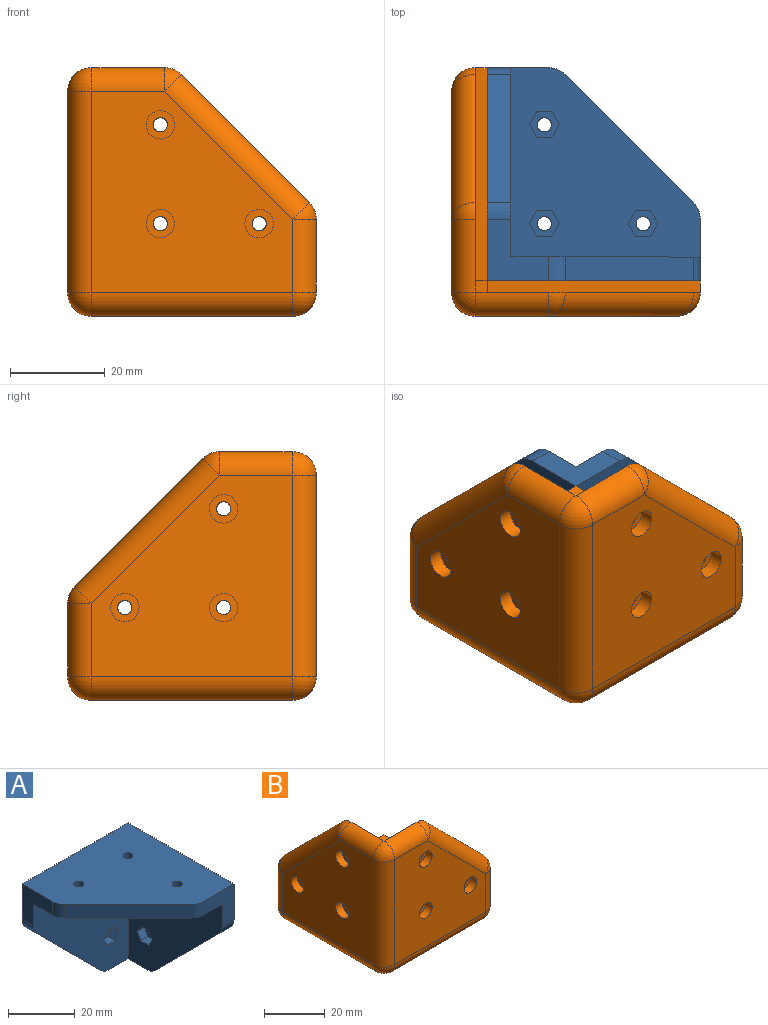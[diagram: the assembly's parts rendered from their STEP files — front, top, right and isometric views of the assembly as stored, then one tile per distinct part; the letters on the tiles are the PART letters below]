
ASSEMBLY  parts=2 mates=1
PART A: 90 faces, bbox 45x45x45 mm
  f0: plane 40x40mm, normal (0,0,-1), area 1070.3mm2, adj f1,f2,f3,f5,f9,f57,f58,f59
  f1: plane 40x40mm, normal (0,-1,0), area 1070.3mm2, adj f0,f2,f5,f6,f10,f36,f37,f38
  f2: plane 40x40mm, normal (-1,0,0), area 1070.3mm2, adj f0,f1,f3,f6,f11,f12,f13,f14
  f3: plane 12.93x12.93mm, normal (0,-1,0), area 104.3mm2, adj f0,f2,f4,f7,f84,f89
  f4: plane 45x45mm, normal (1,0,0), area 1552.7mm2, adj f3,f6,f7,f8,f11,f33,f34,f35
  f5: plane 12.93x12.93mm, normal (-1,0,0), area 104.3mm2, adj f0,f1,f7,f8,f86,f88
  f6: plane 12.93x12.93mm, normal (0,0,-1), area 104.3mm2, adj f1,f2,f4,f8,f85,f87
  f7: plane 45x45mm, normal (0,0,1), area 1552.7mm2, adj f3,f4,f5,f8,f9,f78,f79,f80
  f8: plane 45x45mm, normal (0,1,0), area 1552.7mm2, adj f4,f5,f6,f7,f10,f81,f82,f83
  f9: plane 27.07x27.07mm, normal (-0.71,-0.71,0), area 191.4mm2, adj f0,f7,f88,f89
  f10: plane 27.07x27.07mm, normal (-0.71,0,-0.71), area 191.4mm2, adj f1,f8,f86,f87
  f11: plane 27.07x27.07mm, normal (0,-0.71,-0.71), area 191.4mm2, adj f2,f4,f84,f85
  f12: plane 3x2.75mm, normal (0,0.87,-0.5), area 9.5mm2, adj f2,f13,f17,f18
  f13: plane 3.18x3mm, normal (0,0,-1), area 9.5mm2, adj f2,f12,f14,f18
  f14: plane 3x2.75mm, normal (0,-0.87,-0.5), area 9.5mm2, adj f2,f13,f15,f18
  f15: plane 3x2.75mm, normal (0,-0.87,0.5), area 9.5mm2, adj f2,f14,f16,f18
  f16: plane 3.18x3mm, normal (0,0,1), area 9.5mm2, adj f2,f15,f17,f18
  f17: plane 3x2.75mm, normal (0,0.87,0.5), area 9.5mm2, adj f2,f12,f16,f18
  f18: plane 6.35x5.5mm, normal (-1,0,0), area 19.1mm2, adj f12,f13,f14,f15,f16,f17,f35
  f19: plane 3.18x3mm, normal (0,0,1), area 9.5mm2, adj f2,f20,f24,f25
  f20: plane 3x2.75mm, normal (0,0.87,0.5), area 9.5mm2, adj f2,f19,f21,f25
  f21: plane 3x2.75mm, normal (0,0.87,-0.5), area 9.5mm2, adj f2,f20,f22,f25
  f22: plane 3.18x3mm, normal (0,0,-1), area 9.5mm2, adj f2,f21,f23,f25
  f23: plane 3x2.75mm, normal (0,-0.87,-0.5), area 9.5mm2, adj f2,f22,f24,f25
  f24: plane 3x2.75mm, normal (0,-0.87,0.5), area 9.5mm2, adj f2,f19,f23,f25
  f25: plane 6.35x5.5mm, normal (-1,0,0), area 19.1mm2, adj f19,f20,f21,f22,f23,f24,f34
  f26: plane 3x2.75mm, normal (0,-0.87,0.5), area 9.5mm2, adj f2,f27,f31,f32
  f27: plane 3.18x3mm, normal (0,0,1), area 9.5mm2, adj f2,f26,f28,f32
  f28: plane 3x2.75mm, normal (0,0.87,0.5), area 9.5mm2, adj f2,f27,f29,f32
  f29: plane 3x2.75mm, normal (0,0.87,-0.5), area 9.5mm2, adj f2,f28,f30,f32
  f30: plane 3.18x3mm, normal (0,0,-1), area 9.5mm2, adj f2,f29,f31,f32
  f31: plane 3x2.75mm, normal (0,-0.87,-0.5), area 9.5mm2, adj f2,f26,f30,f32
  f32: plane 6.35x5.5mm, normal (-1,0,0), area 19.1mm2, adj f26,f27,f28,f29,f30,f31,f33
  f33: cylinder r=1.5mm len=3mm, axis (-1,0,0), area 18.8mm2, adj f4,f32
  f34: cylinder r=1.5mm len=3mm, axis (-1,0,0), area 18.8mm2, adj f4,f25
  f35: cylinder r=1.5mm len=3mm, axis (-1,0,0), area 18.8mm2, adj f4,f18
  f36: plane 3x2.75mm, normal (0.87,0,-0.5), area 9.5mm2, adj f1,f37,f41,f42
  f37: plane 3x2.75mm, normal (0.87,0,0.5), area 9.5mm2, adj f1,f36,f38,f42
  f38: plane 3.18x3mm, normal (0,0,1), area 9.5mm2, adj f1,f37,f39,f42
  f39: plane 3x2.75mm, normal (-0.87,0,0.5), area 9.5mm2, adj f1,f38,f40,f42
  f40: plane 3x2.75mm, normal (-0.87,0,-0.5), area 9.5mm2, adj f1,f39,f41,f42
  f41: plane 3.18x3mm, normal (0,0,-1), area 9.5mm2, adj f1,f36,f40,f42
  f42: plane 6.35x5.5mm, normal (0,-1,0), area 19.1mm2, adj f36,f37,f38,f39,f40,f41,f83
  f43: plane 3.18x3mm, normal (0,0,1), area 9.5mm2, adj f1,f44,f48,f49
  f44: plane 3x2.75mm, normal (-0.87,0,0.5), area 9.5mm2, adj f1,f43,f45,f49
  f45: plane 3x2.75mm, normal (-0.87,0,-0.5), area 9.5mm2, adj f1,f44,f46,f49
  f46: plane 3.18x3mm, normal (0,0,-1), area 9.5mm2, adj f1,f45,f47,f49
  f47: plane 3x2.75mm, normal (0.87,0,-0.5), area 9.5mm2, adj f1,f46,f48,f49
  f48: plane 3x2.75mm, normal (0.87,0,0.5), area 9.5mm2, adj f1,f43,f47,f49
  f49: plane 6.35x5.5mm, normal (0,-1,0), area 19.1mm2, adj f43,f44,f45,f46,f47,f48,f82
  f50: plane 3x2.75mm, normal (-0.87,0,0.5), area 9.5mm2, adj f1,f51,f55,f56
  f51: plane 3x2.75mm, normal (-0.87,0,-0.5), area 9.5mm2, adj f1,f50,f52,f56
  f52: plane 3.18x3mm, normal (0,0,-1), area 9.5mm2, adj f1,f51,f53,f56
  f53: plane 3x2.75mm, normal (0.87,0,-0.5), area 9.5mm2, adj f1,f52,f54,f56
  f54: plane 3x2.75mm, normal (0.87,0,0.5), area 9.5mm2, adj f1,f53,f55,f56
  f55: plane 3.18x3mm, normal (0,0,1), area 9.5mm2, adj f1,f50,f54,f56
  f56: plane 6.35x5.5mm, normal (0,-1,0), area 19.1mm2, adj f50,f51,f52,f53,f54,f55,f81
  f57: plane 3x2.75mm, normal (-0.5,0.87,0), area 9.5mm2, adj f0,f58,f62,f63
  f58: plane 3x2.75mm, normal (0.5,0.87,0), area 9.5mm2, adj f0,f57,f59,f63
  f59: plane 3.18x3mm, normal (1,0,0), area 9.5mm2, adj f0,f58,f60,f63
  f60: plane 3x2.75mm, normal (0.5,-0.87,0), area 9.5mm2, adj f0,f59,f61,f63
  f61: plane 3x2.75mm, normal (-0.5,-0.87,0), area 9.5mm2, adj f0,f60,f62,f63
  f62: plane 3.18x3mm, normal (-1,0,0), area 9.5mm2, adj f0,f57,f61,f63
  f63: plane 6.35x5.5mm, normal (0,0,-1), area 19.1mm2, adj f57,f58,f59,f60,f61,f62,f80
  f64: plane 3.18x3mm, normal (1,0,0), area 9.5mm2, adj f0,f65,f69,f70
  f65: plane 3x2.75mm, normal (0.5,-0.87,0), area 9.5mm2, adj f0,f64,f66,f70
  f66: plane 3x2.75mm, normal (-0.5,-0.87,0), area 9.5mm2, adj f0,f65,f67,f70
  f67: plane 3.18x3mm, normal (-1,0,0), area 9.5mm2, adj f0,f66,f68,f70
  f68: plane 3x2.75mm, normal (-0.5,0.87,0), area 9.5mm2, adj f0,f67,f69,f70
  f69: plane 3x2.75mm, normal (0.5,0.87,0), area 9.5mm2, adj f0,f64,f68,f70
  f70: plane 6.35x5.5mm, normal (0,0,-1), area 19.1mm2, adj f64,f65,f66,f67,f68,f69,f79
  f71: plane 3x2.75mm, normal (0.5,-0.87,0), area 9.5mm2, adj f0,f72,f76,f77
  f72: plane 3x2.75mm, normal (-0.5,-0.87,0), area 9.5mm2, adj f0,f71,f73,f77
  f73: plane 3.18x3mm, normal (-1,0,0), area 9.5mm2, adj f0,f72,f74,f77
  f74: plane 3x2.75mm, normal (-0.5,0.87,0), area 9.5mm2, adj f0,f73,f75,f77
  f75: plane 3x2.75mm, normal (0.5,0.87,0), area 9.5mm2, adj f0,f74,f76,f77
  f76: plane 3.18x3mm, normal (1,0,0), area 9.5mm2, adj f0,f71,f75,f77
  f77: plane 6.35x5.5mm, normal (0,0,-1), area 19.1mm2, adj f71,f72,f73,f74,f75,f76,f78
  f78: cylinder r=1.5mm len=3mm, axis (0,0,-1), area 18.8mm2, adj f7,f77
  f79: cylinder r=1.5mm len=3mm, axis (0,0,-1), area 18.8mm2, adj f7,f70
  f80: cylinder r=1.5mm len=3mm, axis (0,0,-1), area 18.8mm2, adj f7,f63
  f81: cylinder r=1.5mm len=3mm, axis (0,-1,0), area 18.8mm2, adj f8,f56
  f82: cylinder r=1.5mm len=3mm, axis (0,-1,0), area 18.8mm2, adj f8,f49
  f83: cylinder r=1.5mm len=3mm, axis (0,-1,0), area 18.8mm2, adj f8,f42
  f84: cylinder r=5mm len=5mm, axis (-1,0,0), area 19.6mm2, adj f2,f3,f4,f11
  f85: cylinder r=5mm len=5mm, axis (-1,0,0), area 19.6mm2, adj f2,f4,f6,f11
  f86: cylinder r=5mm len=5mm, axis (0,-1,0), area 19.6mm2, adj f1,f5,f8,f10
  f87: cylinder r=5mm len=5mm, axis (0,1,0), area 19.6mm2, adj f1,f6,f8,f10
  f88: cylinder r=5mm len=5mm, axis (0,0,1), area 19.6mm2, adj f0,f5,f7,f9
  f89: cylinder r=5mm len=5mm, axis (0,0,-1), area 19.6mm2, adj f0,f3,f7,f9
PART B: 64 faces, bbox 52.5x52.5x52.5 mm
  f0: cylinder r=1.5mm len=3mm, axis (0,1,0), area 18.8mm2, adj f16,f41
  f1: cylinder r=1.5mm len=3mm, axis (0,1,0), area 18.8mm2, adj f16,f39
  f2: cylinder r=1.5mm len=3mm, axis (0,1,0), area 18.8mm2, adj f16,f37
  f3: cylinder r=1.5mm len=3mm, axis (1,0,0), area 18.8mm2, adj f15,f35
  f4: cylinder r=1.5mm len=3mm, axis (1,0,0), area 18.8mm2, adj f15,f33
  f5: cylinder r=1.5mm len=3mm, axis (1,0,0), area 18.8mm2, adj f15,f31
  f6: cylinder r=1.5mm len=3mm, axis (0,0,1), area 18.8mm2, adj f17,f29
  f7: cylinder r=1.5mm len=3mm, axis (0,0,1), area 18.8mm2, adj f17,f27
  f8: cylinder r=1.5mm len=3mm, axis (0,0,1), area 18.8mm2, adj f17,f25
  f9: plane 2.5x2.5mm, normal (0,0,1), area 6.3mm2, adj f20,f21,f54,f59
  f10: plane 42.5x42.5mm, normal (0,-1,0), area 1355mm2, adj f36,f38,f40,f53,f56,f59,f60,f63
  f11: plane 2.5x2.5mm, normal (1,0,0), area 6.3mm2, adj f22,f23,f55,f60
  f12: plane 42.5x42.5mm, normal (0,0,-1), area 1355mm2, adj f24,f26,f28,f42,f48,f49,f55,f56
  f13: plane 2.5x2.5mm, normal (0,1,0), area 6.3mm2, adj f18,f19,f42,f43
  f14: plane 42.5x42.5mm, normal (-1,0,0), area 1355mm2, adj f30,f32,f34,f43,f47,f49,f53,f54
  f15: plane 45x45mm, normal (1,0,0), area 1552.7mm2, adj f3,f4,f5,f19,f20,f43,f44,f47
  f16: plane 45x45mm, normal (0,1,0), area 1552.7mm2, adj f0,f1,f2,f21,f23,f59,f60,f61
  f17: plane 45x45mm, normal (0,0,1), area 1552.7mm2, adj f6,f7,f8,f18,f22,f42,f45,f48
  f18: plane 45x2.5mm, normal (1,0,0), area 112.5mm2, adj f13,f17,f19,f22
  f19: plane 45x2.5mm, normal (0,0,1), area 112.5mm2, adj f13,f15,f18,f20
  f20: plane 45x2.5mm, normal (0,1,0), area 112.5mm2, adj f9,f15,f19,f21
  f21: plane 45x2.5mm, normal (1,0,0), area 112.5mm2, adj f9,f16,f20,f23
  f22: plane 45x2.5mm, normal (0,1,0), area 112.5mm2, adj f11,f17,f18,f23
  f23: plane 45x2.5mm, normal (0,0,1), area 112.5mm2, adj f11,f16,f21,f22
  f24: cylinder r=3mm len=6mm, axis (0,0,-1), area 56.5mm2, adj f12,f25
  f25: plane 6x6mm, normal (0,0,-1), area 21.2mm2, adj f8,f24
  f26: cylinder r=3mm len=6mm, axis (0,0,-1), area 56.5mm2, adj f12,f27
  f27: plane 6x6mm, normal (0,0,-1), area 21.2mm2, adj f7,f26
  f28: cylinder r=3mm len=6mm, axis (0,0,-1), area 56.5mm2, adj f12,f29
  f29: plane 6x6mm, normal (0,0,-1), area 21.2mm2, adj f6,f28
  f30: cylinder r=3mm len=6mm, axis (-1,0,0), area 56.5mm2, adj f14,f31
  f31: plane 6x6mm, normal (-1,0,0), area 21.2mm2, adj f5,f30
  f32: cylinder r=3mm len=6mm, axis (-1,0,0), area 56.5mm2, adj f14,f33
  f33: plane 6x6mm, normal (-1,0,0), area 21.2mm2, adj f4,f32
  f34: cylinder r=3mm len=6mm, axis (-1,0,0), area 56.5mm2, adj f14,f35
  f35: plane 6x6mm, normal (-1,0,0), area 21.2mm2, adj f3,f34
  f36: cylinder r=3mm len=6mm, axis (0,-1,0), area 56.5mm2, adj f10,f37
  f37: plane 6x6mm, normal (0,-1,0), area 21.2mm2, adj f2,f36
  f38: cylinder r=3mm len=6mm, axis (0,-1,0), area 56.5mm2, adj f10,f39
  f39: plane 6x6mm, normal (0,-1,0), area 21.2mm2, adj f1,f38
  f40: cylinder r=3mm len=6mm, axis (0,-1,0), area 56.5mm2, adj f10,f41
  f41: plane 6x6mm, normal (0,-1,0), area 21.2mm2, adj f0,f40
  f42: cylinder r=5mm len=15.43mm, axis (-1,0,0), area 121.2mm2, adj f12,f13,f17,f45,f46
  f43: cylinder r=5mm len=15.43mm, axis (0,0,-1), area 121.2mm2, adj f13,f14,f15,f44,f46
  f44: sphere r=5mm, area 19.6mm2, adj f15,f43,f47
  f45: sphere r=5mm, area 19.6mm2, adj f17,f42,f48
  f46: sphere r=5mm, area 39.3mm2, adj f42,f43,f49
  f47: cylinder r=5mm len=30.61mm, axis (0,-0.71,0.71), area 300.7mm2, adj f14,f15,f44,f50
  f48: cylinder r=5mm len=30.61mm, axis (-0.71,0.71,0), area 300.7mm2, adj f12,f17,f45,f51
  f49: cylinder r=5mm len=42.5mm, axis (0,-1,0), area 333.8mm2, adj f12,f14,f46,f52
  f50: sphere r=5mm, area 19.6mm2, adj f15,f47,f54
  f51: sphere r=5mm, area 19.6mm2, adj f17,f48,f55
  f52: sphere r=5mm, area 39.3mm2, adj f49,f53,f56
  f53: cylinder r=5mm len=42.5mm, axis (0,0,1), area 333.8mm2, adj f10,f14,f52,f57
  f54: cylinder r=5mm len=15.43mm, axis (0,1,0), area 121.2mm2, adj f9,f14,f15,f50,f57
  f55: cylinder r=5mm len=15.43mm, axis (0,1,0), area 121.2mm2, adj f11,f12,f17,f51,f58
  f56: cylinder r=5mm len=42.5mm, axis (1,0,0), area 333.8mm2, adj f10,f12,f52,f58
  f57: sphere r=5mm, area 39.3mm2, adj f53,f54,f59
  f58: sphere r=5mm, area 39.3mm2, adj f55,f56,f60
  f59: cylinder r=5mm len=15.43mm, axis (-1,0,0), area 121.2mm2, adj f9,f10,f16,f57,f61
  f60: cylinder r=5mm len=15.43mm, axis (0,0,-1), area 121.2mm2, adj f10,f11,f16,f58,f62
  f61: sphere r=5mm, area 19.6mm2, adj f16,f59,f63
  f62: sphere r=5mm, area 19.6mm2, adj f16,f60,f63
  f63: cylinder r=5mm len=30.61mm, axis (0.71,0,-0.71), area 300.7mm2, adj f10,f16,f61,f62
PLACE A rot(axis=(-0.71,0.71,0),180deg) t=(47.5,52.5,47.5)mm
PLACE B t=(-5,0,-5)mm
MATE fastened A.f7 <-> B.f19  axis (0,0,-1) through (2.5,7.5,2.5)mm
